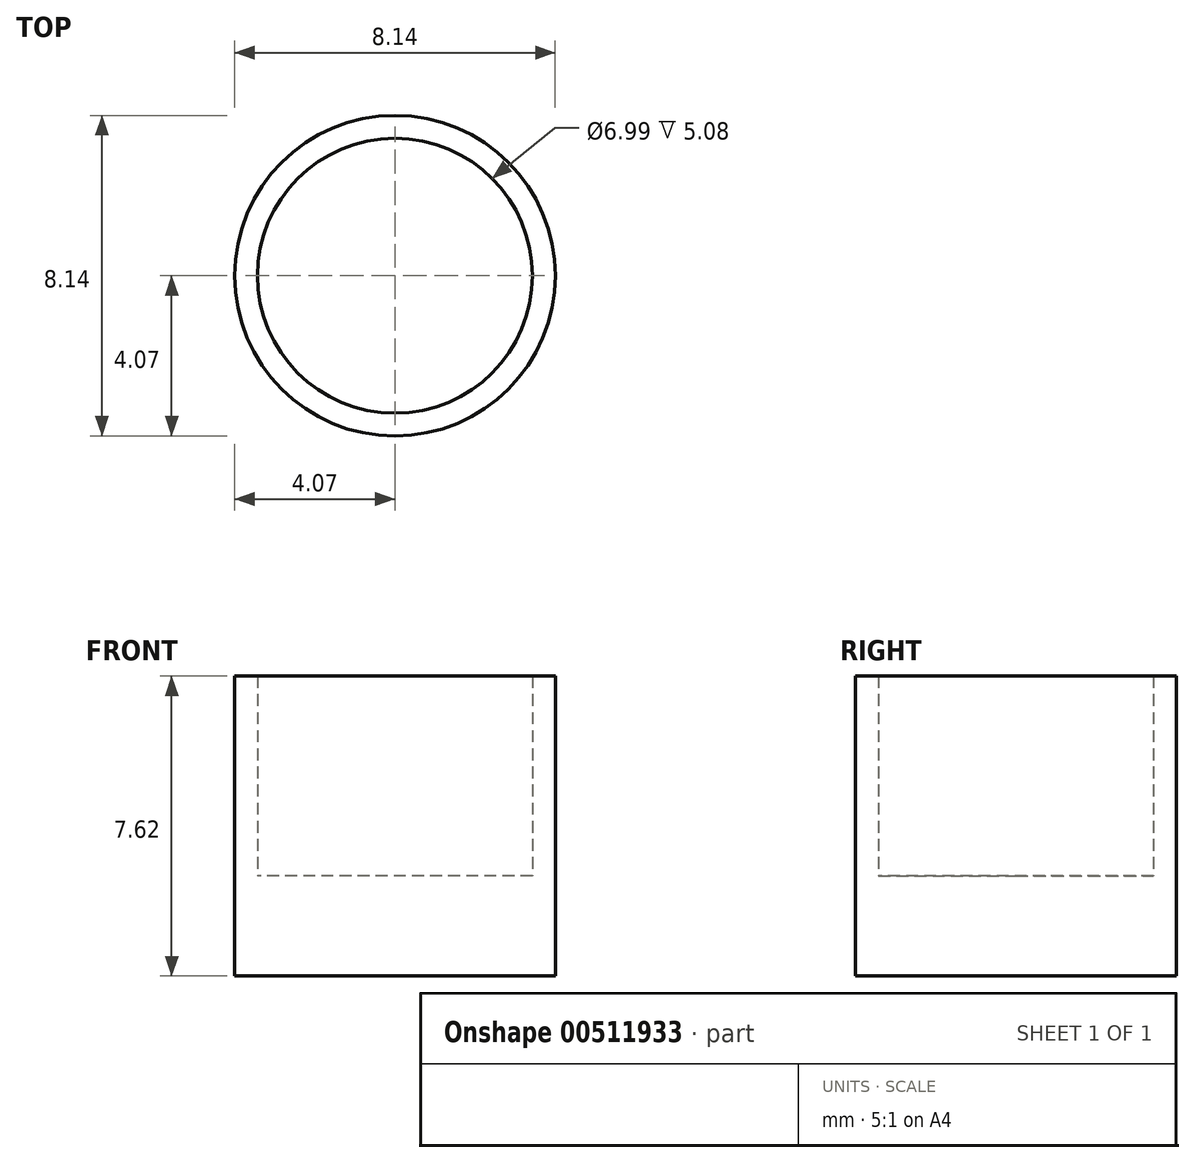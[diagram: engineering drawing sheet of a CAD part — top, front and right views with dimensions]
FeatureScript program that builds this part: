
annotation { "Feature Type Name" : "Feature", "Feature Type Description" : "" }
export const myFeature = defineFeature(function(context is Context, id is Id, definition is map)
    precondition{}
    {
        {
            var Q0;
            Q0=qCreatedBy(makeId("Top.planeOp"),FACE);
            var sketch = newSketch(context, id + "F0", { "sketchPlane" : qUnion([Q0])});
            skCircle(sketch, "E0", {"center": v(0, 0) * mm, "radius": 3.5 * mm});
            skSolve(sketch);
        }
        {
            var Q0;
            Q0=qCreatedBy(makeId("Top.planeOp"),FACE);
            var sketch = newSketch(context, id + "F1", { "sketchPlane" : qUnion([Q0])});
            skCircle(sketch, "E1", {"center": v(0, 0) * mm, "radius": 4.07 * mm});
            skSolve(sketch);
        }
        {
            var Q0;
            Q0 = qSketchRegion(id + "F1", true);
            extrude(context, id + "F2", {"entities" : qUnion([Q0]), "depth" : 7.62 * mm});
        }
        {
            var Q0;
            Q0=sQuery(id+"F0.wireOp",VERTEX,"E0.center");
            var Q1;
            Q1=makeQuery(id+"F2.opExtrude","SWEPT_BODY",BODY,{"disambiguationData":[OSD([sQuery(id+"F1.wireOp",EDGE,"E1")])]});
            hole(context, id + "F3", {"style" : HoleStyle.SIMPLE, "endStyle" : HoleEndStyle.THROUGH, "oppositeDirection" : true, "holeDiameter" : 7 * mm, "isTappedThrough" : true, "tappedDepth" : 12.7 * mm, "tapClearance" : 3, "locations" : qUnion([Q0]), "scope" : qUnion([Q1])});
        }
        {
            var Q0;
            Q0=qCreatedBy(makeId("Top.planeOp"),FACE);
            var sketch = newSketch(context, id + "F4", { "sketchPlane" : qUnion([Q0])});
            skCircle(sketch, "E2", {"center": v(0, 0) * mm, "radius": 4.01 * mm});
            skSolve(sketch);
        }
        {
            var Q0;
            Q0 = qSketchRegion(id + "F4", true);
            extrude(context, id + "F5", {"entities" : qUnion([Q0]), "operationType" : NewBodyOperationType.ADD, "depth" : 2.54 * mm});
        }
    });
